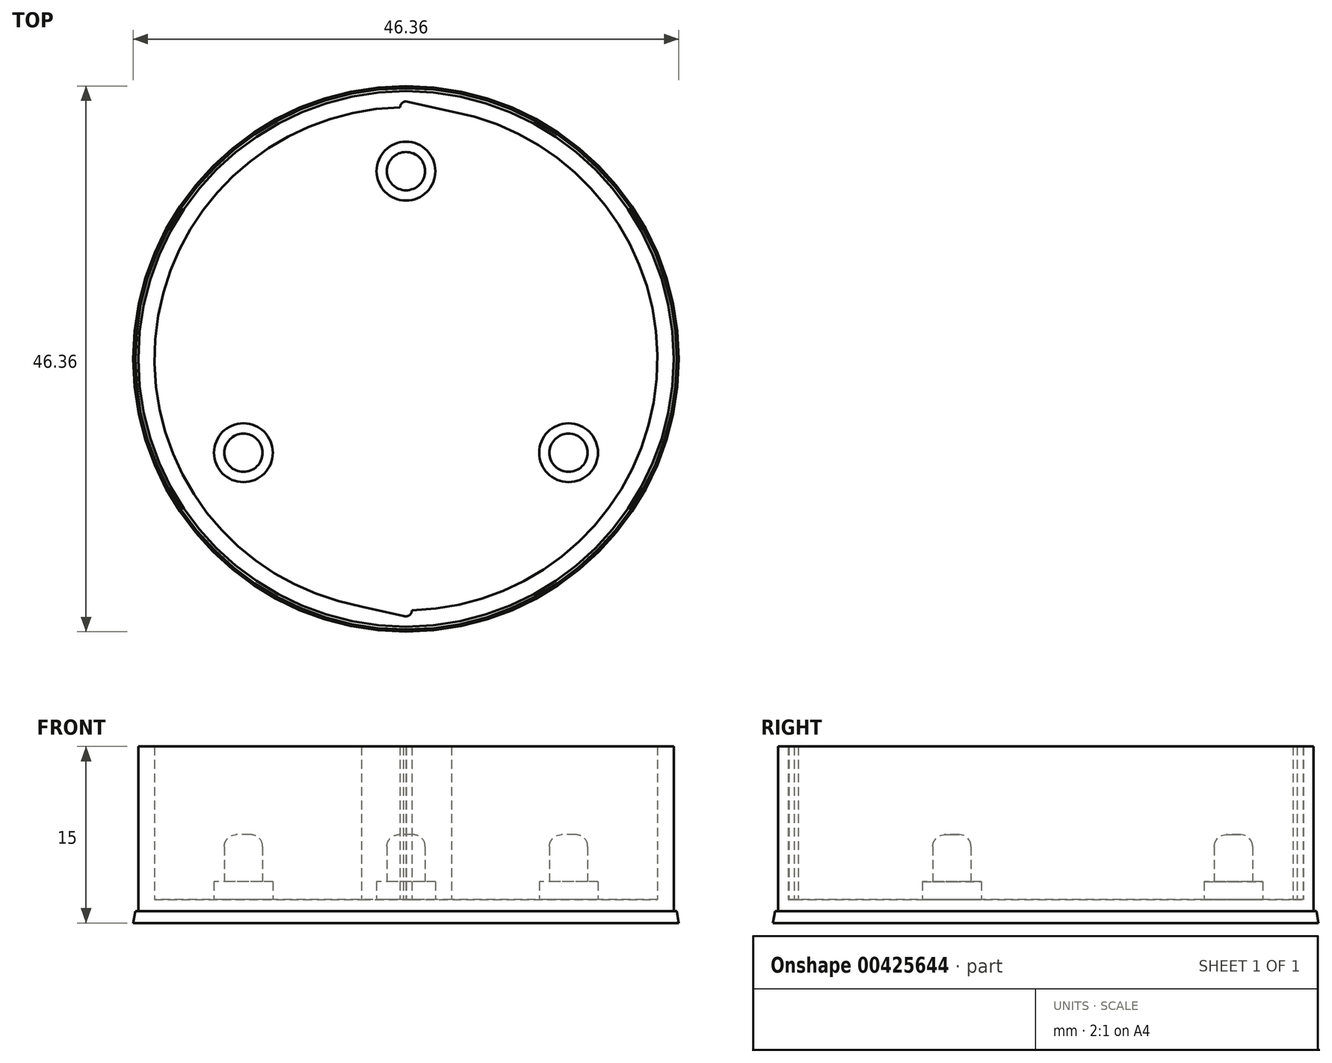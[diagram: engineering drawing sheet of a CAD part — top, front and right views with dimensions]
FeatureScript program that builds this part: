
annotation { "Feature Type Name" : "Feature", "Feature Type Description" : "" }
export const myFeature = defineFeature(function(context is Context, id is Id, definition is map)
    precondition{}
    {
        {
            var Q0;
            Q0=qCreatedBy(makeId("Top.planeOp"),FACE);
            var sketch = newSketch(context, id + "F0", { "sketchPlane" : qUnion([Q0])});
            skCircle(sketch, "E0", {"center": v(0, 0) * mm, "radius": 20.25 * mm});
            skSolve(sketch);
        }
        {
            var Q0;
            Q0=qSketchRegion(id+"F0",true);
            extrude(context, id + "F1", {"entities" : qUnion([Q0]), "depth" : 1 * mm});
        }
        {
            var Q0;
            Q0=makeQuery(id+"F1.opExtrude","CAP_FACE",FACE,{"disambiguationData":[OSD([sQuery(id+"F0.wireOp",EDGE,"E0")])],"isStart":false});
            var sketch = newSketch(context, id + "F2", { "sketchPlane" : qUnion([Q0])});
            skCircle(sketch, "E1.cCircle", {"center": v(0, 0) * mm, "radius": 15.95 * mm, "construction": true});
            skLineSegment(sketch, "E1.0", {"start": v(0, 15.95) * mm, "end": v(13.81, -7.97) * mm});
            skLineSegment(sketch, "E1.1", {"start": v(13.81, -7.97) * mm, "end": v(-13.81, -7.98) * mm});
            skLineSegment(sketch, "E1.2", {"start": v(-13.81, -7.98) * mm, "end": v(0, 15.95) * mm});
            skCircle(sketch, "E2", {"center": v(0, 15.95) * mm, "radius": 2.5 * mm});
            skCircle(sketch, "E3", {"center": v(-13.81, -7.98) * mm, "radius": 2.5 * mm});
            skCircle(sketch, "E4", {"center": v(13.81, -7.97) * mm, "radius": 2.5 * mm});
            skSolve(sketch);
        }
        {
            var Q0;
            {var subQ0=sQuery(id+"F2.wireOp",EDGE,"E1.2");var subQ1=sQuery(id+"F2.wireOp",EDGE,"E1.0");var subQ2=makeQuery(id+"F2.imprint","INTERSECT",VERTEX,{"derivedFrom":[subQ1,subQ0]});Q0=makeQuery(id+"F2.imprint","IMPRINT",FACE,{"disambiguationData":[TD([[makeQuery(id+"F2.imprint","IMPRINT",EDGE,{"disambiguationData":[TD([[subQ2,-1.0]])],"derivedFrom":subQ1}),-1.0]])]});}
            var Q1;
            {var subQ0=sQuery(id+"F2.wireOp",EDGE,"E1.2");var subQ1=sQuery(id+"F2.wireOp",EDGE,"E1.0");var subQ2=makeQuery(id+"F2.imprint","INTERSECT",VERTEX,{"derivedFrom":[subQ1,subQ0]});Q1=makeQuery(id+"F2.imprint","IMPRINT",FACE,{"disambiguationData":[TD([[makeQuery(id+"F2.imprint","IMPRINT",EDGE,{"disambiguationData":[TD([[subQ2,-1.0]])],"derivedFrom":subQ1}),1.0]])]});}
            var Q2;
            {var subQ0=sQuery(id+"F2.wireOp",EDGE,"E1.1");var subQ1=sQuery(id+"F2.wireOp",EDGE,"E1.0");var subQ2=makeQuery(id+"F2.imprint","INTERSECT",VERTEX,{"derivedFrom":[subQ1,subQ0]});Q2=makeQuery(id+"F2.imprint","IMPRINT",FACE,{"disambiguationData":[TD([[makeQuery(id+"F2.imprint","IMPRINT",EDGE,{"disambiguationData":[TD([[subQ2,1.0]])],"derivedFrom":subQ1}),-1.0]])]});}
            var Q3;
            {var subQ0=sQuery(id+"F2.wireOp",EDGE,"E1.1");var subQ1=sQuery(id+"F2.wireOp",EDGE,"E1.0");var subQ2=makeQuery(id+"F2.imprint","INTERSECT",VERTEX,{"derivedFrom":[subQ1,subQ0]});Q3=makeQuery(id+"F2.imprint","IMPRINT",FACE,{"disambiguationData":[TD([[makeQuery(id+"F2.imprint","IMPRINT",EDGE,{"disambiguationData":[TD([[subQ2,1.0]])],"derivedFrom":subQ1}),1.0]])]});}
            var Q4;
            {var subQ0=sQuery(id+"F2.wireOp",EDGE,"E1.2");var subQ1=sQuery(id+"F2.wireOp",EDGE,"E1.1");var subQ2=makeQuery(id+"F2.imprint","INTERSECT",VERTEX,{"derivedFrom":[subQ1,subQ0]});Q4=makeQuery(id+"F2.imprint","IMPRINT",FACE,{"disambiguationData":[TD([[makeQuery(id+"F2.imprint","IMPRINT",EDGE,{"disambiguationData":[TD([[subQ2,1.0]])],"derivedFrom":subQ1}),-1.0]])]});}
            var Q5;
            {var subQ0=sQuery(id+"F2.wireOp",EDGE,"E1.2");var subQ1=sQuery(id+"F2.wireOp",EDGE,"E1.1");var subQ2=makeQuery(id+"F2.imprint","INTERSECT",VERTEX,{"derivedFrom":[subQ1,subQ0]});Q5=makeQuery(id+"F2.imprint","IMPRINT",FACE,{"disambiguationData":[TD([[makeQuery(id+"F2.imprint","IMPRINT",EDGE,{"disambiguationData":[TD([[subQ2,1.0]])],"derivedFrom":subQ1}),1.0]])]});}
            extrude(context, id + "F3", {"entities" : qUnion([Q0, Q1, Q2, Q3, Q4, Q5]), "operationType" : NewBodyOperationType.ADD, "depth" : 1.5 * mm});
        }
        {
            var Q0;
            Q0=makeQuery(id+"F3.opExtrude","CAP_FACE",FACE,{"disambiguationData":[OSD([sQuery(id+"F2.wireOp",EDGE,"E2")])],"isStart":false});
            var sketch = newSketch(context, id + "F4", { "sketchPlane" : qUnion([Q0])});
            skCircle(sketch, "E5", {"center": v(0, 15.95) * mm, "radius": 1.63 * mm});
            skSolve(sketch);
        }
        {
            var Q0;
            Q0=qSketchRegion(id+"F4",true);
            extrude(context, id + "F5", {"entities" : qUnion([Q0]), "operationType" : NewBodyOperationType.ADD, "depth" : 4 * mm});
        }
        {
            var Q0;
            Q0=makeQuery(id+"F3.opExtrude","CAP_FACE",FACE,{"disambiguationData":[OSD([sQuery(id+"F2.wireOp",EDGE,"E3")])],"isStart":false});
            var sketch = newSketch(context, id + "F6", { "sketchPlane" : qUnion([Q0])});
            skCircle(sketch, "E6", {"center": v(-13.81, -7.98) * mm, "radius": 1.62 * mm});
            skSolve(sketch);
        }
        {
            var Q0;
            Q0=qSketchRegion(id+"F6",true);
            extrude(context, id + "F7", {"entities" : qUnion([Q0]), "operationType" : NewBodyOperationType.ADD, "depth" : 4 * mm});
        }
        {
            var Q0;
            Q0=makeQuery(id+"F3.opExtrude","CAP_FACE",FACE,{"disambiguationData":[OSD([sQuery(id+"F2.wireOp",EDGE,"E4")])],"isStart":false});
            var sketch = newSketch(context, id + "F8", { "sketchPlane" : qUnion([Q0])});
            skCircle(sketch, "E7", {"center": v(13.81, -7.97) * mm, "radius": 1.63 * mm});
            skSolve(sketch);
        }
        {
            var Q0;
            Q0=qSketchRegion(id+"F8",true);
            extrude(context, id + "F9", {"entities" : qUnion([Q0]), "operationType" : NewBodyOperationType.ADD, "depth" : 4 * mm});
        }
        {
            var Q0;
            Q0=makeQuery(id+"F7.opExtrude","CAP_EDGE",EDGE,{"disambiguationData":[OSD([sQuery(id+"F6.wireOp",EDGE,"E6")])],"isStart":false});
            var Q1;
            Q1=makeQuery(id+"F5.opExtrude","CAP_EDGE",EDGE,{"disambiguationData":[OSD([sQuery(id+"F4.wireOp",EDGE,"E5")])],"isStart":false});
            var Q2;
            Q2=makeQuery(id+"F9.opExtrude","CAP_EDGE",EDGE,{"disambiguationData":[OSD([sQuery(id+"F8.wireOp",EDGE,"E7")])],"isStart":false});
            fillet(context, id + "F10", {"entities" : qUnion([Q0, Q1, Q2]), "radius" : 1 * mm, "tangentPropagation" : true, "allowEdgeOverflow" : false});
        }
        {
            var Q0;
            Q0=makeQuery(id+"F1.opExtrude","CAP_FACE",FACE,{"disambiguationData":[OSD([sQuery(id+"F0.wireOp",EDGE,"E0")])],"isStart":false});
            var sketch = newSketch(context, id + "F11", { "sketchPlane" : qUnion([Q0])});
            skLineSegment(sketch, "E8", {"start": v(0, 0) * mm, "end": v(0, -20.25) * mm});
            skLineSegment(sketch, "E9", {"start": v(0, 0) * mm, "end": v(-17.54, 10.12) * mm});
            skLineSegment(sketch, "E10", {"start": v(0, 0) * mm, "end": v(17.54, 10.13) * mm});
            skArc(sketch, "E11", {"start": v(-17.54, 10.12) * mm, "mid": v(-19.2, 6.46) * mm, "end": v(-20.09, 2.54) * mm});
            skArc(sketch, "E12", {"start": v(17.54, 10.13) * mm, "mid": v(15.2, 13.39) * mm, "end": v(12.25, 16.13) * mm});
            skArc(sketch, "E13", {"start": v(0, -20.25) * mm, "mid": v(4, -19.85) * mm, "end": v(7.84, -18.67) * mm});
            skArc(sketch, "E14.0", {"start": v(-19.7, 11.38) * mm, "mid": v(-21.56, 7.26) * mm, "end": v(-22.57, 2.86) * mm});
            skArc(sketch, "E15.0", {"start": v(0, -22.75) * mm, "mid": v(4.5, -22.3) * mm, "end": v(8.81, -20.97) * mm});
            skArc(sketch, "E16.0", {"start": v(19.7, 11.37) * mm, "mid": v(17.07, 15.04) * mm, "end": v(13.76, 18.12) * mm});
            skLineSegment(sketch, "E17", {"start": v(19.7, 11.37) * mm, "end": v(17.54, 10.13) * mm});
            skLineSegment(sketch, "E18", {"start": v(13.76, 18.12) * mm, "end": v(12.25, 16.13) * mm});
            skLineSegment(sketch, "E19", {"start": v(-19.7, 11.38) * mm, "end": v(-17.54, 10.12) * mm});
            skLineSegment(sketch, "E20", {"start": v(-22.57, 2.86) * mm, "end": v(-20.09, 2.54) * mm});
            skLineSegment(sketch, "E21", {"start": v(8.81, -20.97) * mm, "end": v(7.84, -18.67) * mm});
            skLineSegment(sketch, "E22", {"start": v(0, -22.75) * mm, "end": v(0, -20.25) * mm});
            skSolve(sketch);
        }
        {
            var Q0;
            Q0=qSketchRegion(id+"F11",true);
            extrude(context, id + "F12", {"entities" : qUnion([Q0]), "depth" : 3 * mm});
        }
        {
            var Q0;
            Q0=makeQuery(id+"F1.opExtrude","CAP_FACE",FACE,{"disambiguationData":[OSD([sQuery(id+"F0.wireOp",EDGE,"E0")])],"isStart":true});
            var sketch = newSketch(context, id + "F13", { "sketchPlane" : qUnion([Q0])});
            skCircle(sketch, "E23.0", {"center": v(0, 0) * mm, "radius": 22.75 * mm});
            skSolve(sketch);
        }
        {
            var Q0;
            Q0=qSketchRegion(id+"F13",true);
            extrude(context, id + "F14", {"entities" : qUnion([Q0]), "operationType" : NewBodyOperationType.ADD, "oppositeDirection" : true, "depth" : 1 * mm});
        }
        {
            var Q0;
            Q0=makeQuery(id+"F14.boolean.opBoolean","MERGE",FACE,{"derivedFrom":[makeQuery(id+"F1.opExtrude","CAP_FACE",FACE,{"disambiguationData":[OSD([sQuery(id+"F0.wireOp",EDGE,"E0")])],"isStart":false}),makeQuery(id+"F14.opExtrude","CAP_FACE",FACE,{"disambiguationData":[OSD([sQuery(id+"F13.wireOp",EDGE,"E23.0")])],"isStart":false})]});
            var sketch = newSketch(context, id + "F15", { "sketchPlane" : qUnion([Q0])});
            skCircle(sketch, "E24", {"center": v(0, 0) * mm, "radius": 19.75 * mm});
            skCircle(sketch, "E25", {"center": v(0, 0) * mm, "radius": 21.12 * mm});
            skSolve(sketch);
        }
        {
            var Q0;
            Q0=qSketchRegion(id+"F15",true);
            extrude(context, id + "F16", {"entities" : qUnion([Q0]), "operationType" : NewBodyOperationType.REMOVE, "depth" : 3 * mm});
        }
        {
            var Q0;
            Q0=makeQuery(id+"F12.opExtrude","CAP_FACE",FACE,{"disambiguationData":[OSD([sQuery(id+"F11.wireOp",EDGE,"E11"),sQuery(id+"F11.wireOp",EDGE,"E14.0"),sQuery(id+"F11.wireOp",EDGE,"E19"),sQuery(id+"F11.wireOp",EDGE,"E20")])],"isStart":false});
            extrude(context, id + "F17", {"entities" : qUnion([Q0]), "operationType" : NewBodyOperationType.ADD, "depth" : 5 * mm});
        }
        {
            var Q0;
            Q0=makeQuery(id+"F12.opExtrude","CAP_FACE",FACE,{"disambiguationData":[OSD([sQuery(id+"F11.wireOp",EDGE,"E12"),sQuery(id+"F11.wireOp",EDGE,"E16.0"),sQuery(id+"F11.wireOp",EDGE,"E17"),sQuery(id+"F11.wireOp",EDGE,"E18")])],"isStart":false});
            extrude(context, id + "F18", {"entities" : qUnion([Q0]), "operationType" : NewBodyOperationType.ADD, "depth" : 5 * mm});
        }
        {
            var Q0;
            Q0=makeQuery(id+"F12.opExtrude","CAP_FACE",FACE,{"disambiguationData":[OSD([sQuery(id+"F11.wireOp",EDGE,"E13"),sQuery(id+"F11.wireOp",EDGE,"E15.0"),sQuery(id+"F11.wireOp",EDGE,"E21"),sQuery(id+"F11.wireOp",EDGE,"E22")])],"isStart":false});
            extrude(context, id + "F19", {"entities" : qUnion([Q0]), "operationType" : NewBodyOperationType.ADD, "depth" : 5 * mm});
        }
        {
            var Q0;
            Q0=makeQuery(id+"F16.boolean.opBoolean","MERGE",FACE,{"derivedFrom":[makeQuery(id+"F14.boolean.opBoolean","MERGE",FACE,{"derivedFrom":[makeQuery(id+"F1.opExtrude","CAP_FACE",FACE,{"disambiguationData":[OSD([sQuery(id+"F0.wireOp",EDGE,"E0")])],"isStart":false}),makeQuery(id+"F14.opExtrude","CAP_FACE",FACE,{"disambiguationData":[OSD([sQuery(id+"F13.wireOp",EDGE,"E23.0")])],"isStart":false})]}),makeQuery(id+"F16.opExtrude","CAP_FACE",FACE,{"disambiguationData":[OSD([sQuery(id+"F15.wireOp",EDGE,"E24"),sQuery(id+"F15.wireOp",EDGE,"E25")])],"isStart":true})]});
            var sketch = newSketch(context, id + "F20", { "sketchPlane" : qUnion([Q0])});
            skCircle(sketch, "E26", {"center": v(0, 0) * mm, "radius": 21.13 * mm});
            skCircle(sketch, "E27", {"center": v(0, 0) * mm, "radius": 22.75 * mm});
            skLineSegment(sketch, "E28", {"start": v(0, 0) * mm, "end": v(-22.22, -4.9) * mm});
            skLineSegment(sketch, "E29", {"start": v(0, 0) * mm, "end": v(6.87, 21.69) * mm});
            skLineSegment(sketch, "E30", {"start": v(0, 0) * mm, "end": v(15.35, -16.8) * mm});
            skLineSegment(sketch, "E31", {"start": v(0, 0) * mm, "end": v(-22.57, 2.86) * mm});
            skLineSegment(sketch, "E32", {"start": v(0, 0) * mm, "end": v(13.76, 18.12) * mm});
            skLineSegment(sketch, "E33", {"start": v(0, 0) * mm, "end": v(8.81, -20.97) * mm});
            skSolve(sketch);
        }
        {
            var Q0;
            {var subQ1=makeQuery(id+"F12.opExtrude","CAP_EDGE",EDGE,{"disambiguationData":[OSD([sQuery(id+"F11.wireOp",EDGE,"E17")])],"isStart":true});Q0=makeQuery(id+"F20.imprint","IMPRINT",FACE,{"disambiguationData":[TD([[makeQuery(id+"F20.imprint","IMPRINT",EDGE,{"derivedFrom":subQ1}),-1.0]])]});}
            var Q1;
            {var subQ1=makeQuery(id+"F12.opExtrude","CAP_EDGE",EDGE,{"disambiguationData":[OSD([sQuery(id+"F11.wireOp",EDGE,"E19")])],"isStart":true});Q1=makeQuery(id+"F20.imprint","IMPRINT",FACE,{"disambiguationData":[TD([[makeQuery(id+"F20.imprint","IMPRINT",EDGE,{"derivedFrom":subQ1}),1.0]])]});}
            var Q2;
            {var subQ1=makeQuery(id+"F12.opExtrude","CAP_EDGE",EDGE,{"disambiguationData":[OSD([sQuery(id+"F11.wireOp",EDGE,"E19")])],"isStart":true});Q2=makeQuery(id+"F20.imprint","IMPRINT",FACE,{"disambiguationData":[TD([[makeQuery(id+"F20.imprint","IMPRINT",EDGE,{"derivedFrom":subQ1}),-1.0]])]});}
            var Q3;
            {var subQ1=makeQuery(id+"F12.opExtrude","CAP_EDGE",EDGE,{"disambiguationData":[OSD([sQuery(id+"F11.wireOp",EDGE,"E22")])],"isStart":true});Q3=makeQuery(id+"F20.imprint","IMPRINT",FACE,{"disambiguationData":[TD([[makeQuery(id+"F20.imprint","IMPRINT",EDGE,{"derivedFrom":subQ1}),1.0]])]});}
            var Q4;
            {var subQ3=makeQuery(id+"F12.opExtrude","CAP_EDGE",EDGE,{"disambiguationData":[OSD([sQuery(id+"F11.wireOp",EDGE,"E22")])],"isStart":true});Q4=makeQuery(id+"F20.imprint","IMPRINT",FACE,{"disambiguationData":[TD([[makeQuery(id+"F20.imprint","IMPRINT",EDGE,{"derivedFrom":subQ3}),-1.0]])]});}
            var Q5;
            {var subQ1=makeQuery(id+"F12.opExtrude","CAP_EDGE",EDGE,{"disambiguationData":[OSD([sQuery(id+"F11.wireOp",EDGE,"E17")])],"isStart":true});Q5=makeQuery(id+"F20.imprint","IMPRINT",FACE,{"disambiguationData":[TD([[makeQuery(id+"F20.imprint","IMPRINT",EDGE,{"derivedFrom":subQ1}),1.0]])]});}
            extrude(context, id + "F21", {"entities" : qUnion([Q0, Q1, Q2, Q3, Q4, Q5]), "operationType" : NewBodyOperationType.ADD, "depth" : 13 * mm});
        }
        {
            var Q0;
            Q0=makeQuery(id+"F16.boolean.opBoolean","MERGE",FACE,{"derivedFrom":[makeQuery(id+"F14.boolean.opBoolean","MERGE",FACE,{"derivedFrom":[makeQuery(id+"F1.opExtrude","CAP_FACE",FACE,{"disambiguationData":[OSD([sQuery(id+"F0.wireOp",EDGE,"E0")])],"isStart":false}),makeQuery(id+"F14.opExtrude","CAP_FACE",FACE,{"disambiguationData":[OSD([sQuery(id+"F13.wireOp",EDGE,"E23.0")])],"isStart":false})]}),makeQuery(id+"F16.opExtrude","CAP_FACE",FACE,{"disambiguationData":[OSD([sQuery(id+"F15.wireOp",EDGE,"E24"),sQuery(id+"F15.wireOp",EDGE,"E25")])],"isStart":true})]});
            var sketch = newSketch(context, id + "F22", { "sketchPlane" : qUnion([Q0])});
            skCircle(sketch, "E34", {"center": v(0, 0) * mm, "radius": 21.38 * mm});
            skCircle(sketch, "E35", {"center": v(0, 0) * mm, "radius": 20.52 * mm});
            skSolve(sketch);
        }
        {
            var Q0;
            Q0=qSketchRegion(id+"F22",true);
            extrude(context, id + "F23", {"entities" : qUnion([Q0]), "operationType" : NewBodyOperationType.REMOVE, "depth" : 25 * mm});
        }
        {
            var Q0;
            Q0=makeQuery(id+"F23.boolean.opBoolean","MERGE",FACE,{"derivedFrom":[makeQuery(id+"F16.boolean.opBoolean","MERGE",FACE,{"derivedFrom":[makeQuery(id+"F14.boolean.opBoolean","MERGE",FACE,{"derivedFrom":[makeQuery(id+"F1.opExtrude","CAP_FACE",FACE,{"disambiguationData":[OSD([sQuery(id+"F0.wireOp",EDGE,"E0")])],"isStart":false}),makeQuery(id+"F14.opExtrude","CAP_FACE",FACE,{"disambiguationData":[OSD([sQuery(id+"F13.wireOp",EDGE,"E23.0")])],"isStart":false})]}),makeQuery(id+"F16.opExtrude","CAP_FACE",FACE,{"disambiguationData":[OSD([sQuery(id+"F15.wireOp",EDGE,"E24"),sQuery(id+"F15.wireOp",EDGE,"E25")])],"isStart":true})]}),makeQuery(id+"F23.opExtrude","CAP_FACE",FACE,{"disambiguationData":[OSD([sQuery(id+"F22.wireOp",EDGE,"E34"),sQuery(id+"F22.wireOp",EDGE,"E35")])],"isStart":true})]});
            var sketch = newSketch(context, id + "F24", { "sketchPlane" : qUnion([Q0])});
            skCircle(sketch, "E36", {"center": v(0, 0) * mm, "radius": 21.38 * mm});
            skCircle(sketch, "E37", {"center": v(0, 0) * mm, "radius": 22.75 * mm});
            skSolve(sketch);
        }
        {
            var Q0;
            Q0=qSketchRegion(id+"F24",true);
            extrude(context, id + "F25", {"entities" : qUnion([Q0]), "operationType" : NewBodyOperationType.ADD, "depth" : 13 * mm});
        }
        {
            var Q0;
            Q0=makeQuery(id+"F23.boolean.opBoolean","MERGE",FACE,{"derivedFrom":[makeQuery(id+"F16.boolean.opBoolean","MERGE",FACE,{"derivedFrom":[makeQuery(id+"F14.boolean.opBoolean","MERGE",FACE,{"derivedFrom":[makeQuery(id+"F1.opExtrude","CAP_FACE",FACE,{"disambiguationData":[OSD([sQuery(id+"F0.wireOp",EDGE,"E0")])],"isStart":false}),makeQuery(id+"F14.opExtrude","CAP_FACE",FACE,{"disambiguationData":[OSD([sQuery(id+"F13.wireOp",EDGE,"E23.0")])],"isStart":false})]}),makeQuery(id+"F16.opExtrude","CAP_FACE",FACE,{"disambiguationData":[OSD([sQuery(id+"F15.wireOp",EDGE,"E24"),sQuery(id+"F15.wireOp",EDGE,"E25")])],"isStart":true})]}),makeQuery(id+"F23.opExtrude","CAP_FACE",FACE,{"disambiguationData":[OSD([sQuery(id+"F22.wireOp",EDGE,"E34"),sQuery(id+"F22.wireOp",EDGE,"E35")])],"isStart":true})]});
            var sketch = newSketch(context, id + "F26", { "sketchPlane" : qUnion([Q0])});
            skLineSegment(sketch, "E38", {"start": v(0, 0) * mm, "end": v(0, -21.38) * mm});
            skCircle(sketch, "E39", {"center": v(0, -21.38) * mm, "radius": 0.5 * mm});
            skLineSegment(sketch, "E40", {"start": v(0, 0) * mm, "end": v(0, 21.38) * mm});
            skCircle(sketch, "E41", {"center": v(0, 21.38) * mm, "radius": 0.5 * mm});
            skSolve(sketch);
        }
        {
            var Q0;
            Q0 = qSketchRegion(id + "F26", true);
            extrude(context, id + "F27", {"entities" : qUnion([Q0]), "operationType" : NewBodyOperationType.REMOVE, "depth" : 25 * mm});
        }
        {
            var Q0;
            Q0 = qSketchRegion(id + "F26", true);
            extrude(context, id + "F28", {"entities" : qUnion([Q0]), "operationType" : NewBodyOperationType.REMOVE, "depth" : 25 * mm});
        }
        {
            var Q0;
            Q0=makeQuery(id+"F27.boolean.opBoolean","MERGE",FACE,{"derivedFrom":[makeQuery(id+"F23.boolean.opBoolean","MERGE",FACE,{"derivedFrom":[makeQuery(id+"F16.boolean.opBoolean","MERGE",FACE,{"derivedFrom":[makeQuery(id+"F14.boolean.opBoolean","MERGE",FACE,{"derivedFrom":[makeQuery(id+"F1.opExtrude","CAP_FACE",FACE,{"disambiguationData":[OSD([sQuery(id+"F0.wireOp",EDGE,"E0")])],"isStart":false}),makeQuery(id+"F14.opExtrude","CAP_FACE",FACE,{"disambiguationData":[OSD([sQuery(id+"F13.wireOp",EDGE,"E23.0")])],"isStart":false})]}),makeQuery(id+"F16.opExtrude","CAP_FACE",FACE,{"disambiguationData":[OSD([sQuery(id+"F15.wireOp",EDGE,"E24"),sQuery(id+"F15.wireOp",EDGE,"E25")])],"isStart":true})]}),makeQuery(id+"F23.opExtrude","CAP_FACE",FACE,{"disambiguationData":[OSD([sQuery(id+"F22.wireOp",EDGE,"E34"),sQuery(id+"F22.wireOp",EDGE,"E35")])],"isStart":true})]}),makeQuery(id+"F27.opExtrude","CAP_FACE",FACE,{"disambiguationData":[OSD([sQuery(id+"F26.wireOp",EDGE,"E39")])],"isStart":true}),makeQuery(id+"F27.opExtrude","CAP_FACE",FACE,{"disambiguationData":[OSD([sQuery(id+"F26.wireOp",EDGE,"E41")])],"isStart":true})]});
            var sketch = newSketch(context, id + "F29", { "sketchPlane" : qUnion([Q0])});
            skLineSegment(sketch, "E42", {"start": v(0.5, 21.37) * mm, "end": v(5.45, 20.67) * mm});
            skLineSegment(sketch, "E43", {"start": v(5.45, 20.67) * mm, "end": v(0, 21.89) * mm});
            skPoint(sketch, "E43.endSnap0", {"position": v(0, 21.88) * mm});
            skLineSegment(sketch, "E44", {"start": v(0, 21.89) * mm, "end": v(0.5, 21.37) * mm});
            skLineSegment(sketch, "E45", {"start": v(-0.5, -21.37) * mm, "end": v(-5.45, -20.67) * mm});
            skLineSegment(sketch, "E46", {"start": v(-5.45, -20.67) * mm, "end": v(0, -21.88) * mm});
            skLineSegment(sketch, "E47", {"start": v(0, -21.88) * mm, "end": v(-0.5, -21.37) * mm});
            skSolve(sketch);
        }
        {
            var Q0;
            Q0 = qSketchRegion(id + "F29", true);
            extrude(context, id + "F30", {"entities" : qUnion([Q0]), "operationType" : NewBodyOperationType.REMOVE, "depth" : 25 * mm});
        }
        {
            var Q0;
            Q0=makeQuery(id+"F14.boolean.opBoolean","MERGE",FACE,{"derivedFrom":[makeQuery(id+"F1.opExtrude","CAP_FACE",FACE,{"disambiguationData":[OSD([sQuery(id+"F0.wireOp",EDGE,"E0")])],"isStart":true}),makeQuery(id+"F14.opExtrude","CAP_FACE",FACE,{"disambiguationData":[OSD([sQuery(id+"F13.wireOp",EDGE,"E23.0")])],"isStart":true})]});
            var sketch = newSketch(context, id + "F31", { "sketchPlane" : qUnion([Q0])});
            skCircle(sketch, "E48", {"center": v(0, 0) * mm, "radius": 23 * mm});
            skSolve(sketch);
        }
        {
            var Q0;
            Q0 = qSketchRegion(id + "F31", true);
            extrude(context, id + "F32", {"entities" : qUnion([Q0]), "operationType" : NewBodyOperationType.ADD, "depth" : 1 * mm, "hasDraft" : true, "draftAngle" : 10 * degree});
        }
    });
